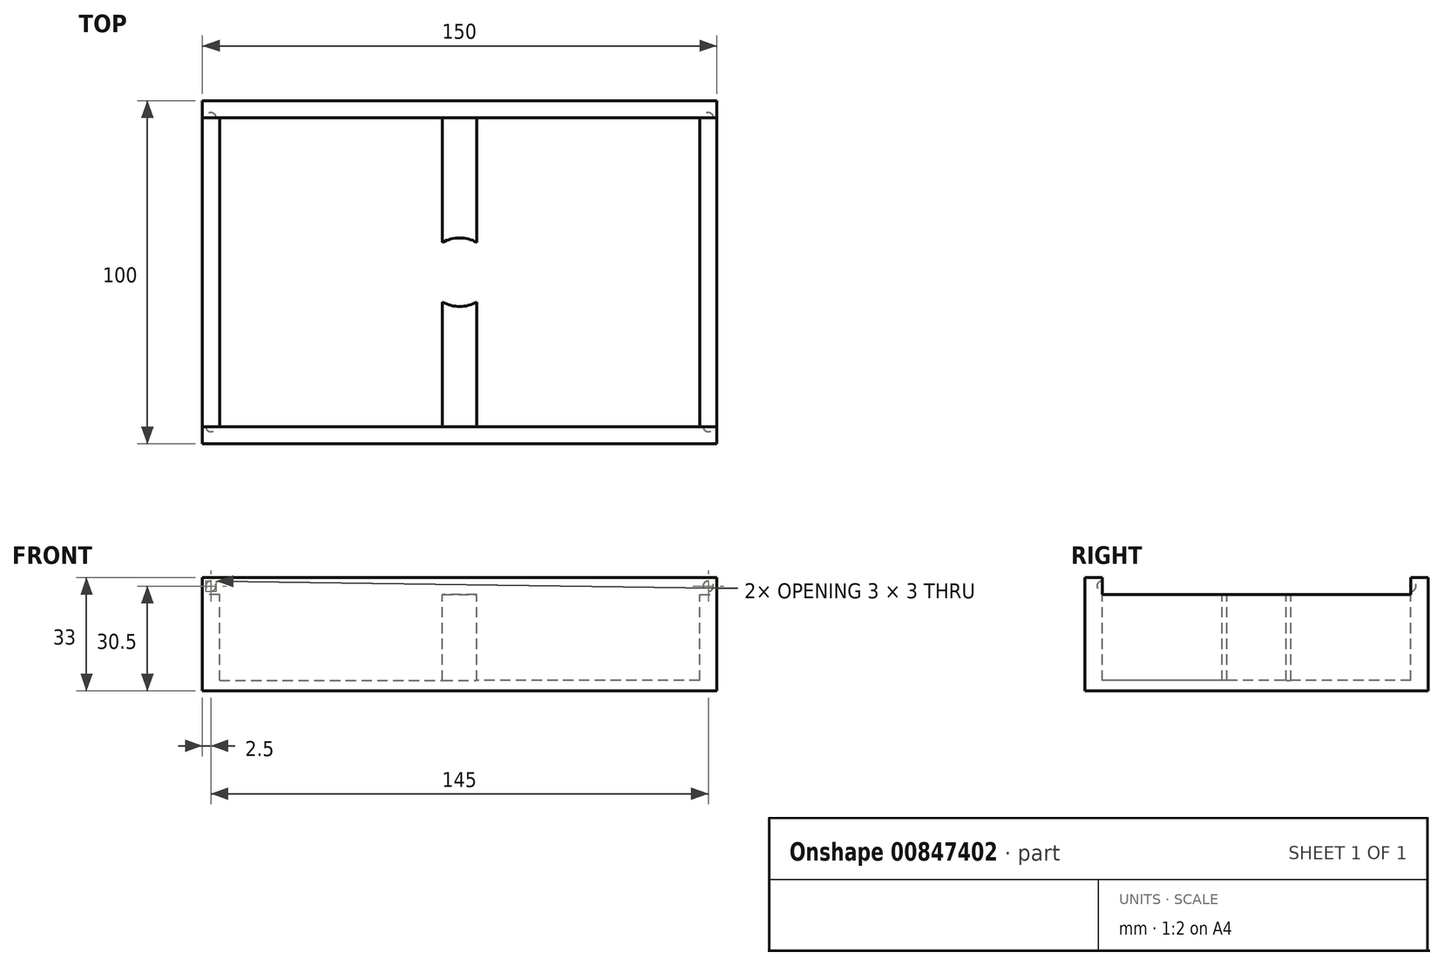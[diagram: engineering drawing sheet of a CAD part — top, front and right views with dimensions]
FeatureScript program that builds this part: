
annotation { "Feature Type Name" : "Feature", "Feature Type Description" : "" }
export const myFeature = defineFeature(function(context is Context, id is Id, definition is map)
    precondition{}
    {
        {
            var Q0;
            Q0=qCreatedBy(makeId("Top.planeOp"),FACE);
            var sketch = newSketch(context, id + "F0", { "sketchPlane" : qUnion([Q0])});
            skLineSegment(sketch, "E0.bottom", {"start": v(75, -50) * mm, "end": v(-75, -50) * mm});
            skLineSegment(sketch, "E0.top", {"start": v(75, 50) * mm, "end": v(-75, 50) * mm});
            skLineSegment(sketch, "E0.left", {"start": v(75, -50) * mm, "end": v(75, 50) * mm});
            skLineSegment(sketch, "E0.right", {"start": v(-75, -50) * mm, "end": v(-75, 50) * mm});
            skPoint(sketch, "E0.middle", {"position": v(0, 0) * mm});
            skSolve(sketch);
        }
        {
            var Q0;
            Q0=qSketchRegion(id+"F0",true);
            extrude(context, id + "F1", {"entities" : qUnion([Q0]), "depth" : 33 * mm, "offsetDistance" : 25 * mm});
        }
        {
            var Q0;
            Q0=makeQuery(id+"F1.opExtrude","CAP_FACE",FACE,{"disambiguationData":[OSD([sQuery(id+"F0.wireOp",EDGE,"E0.bottom"),sQuery(id+"F0.wireOp",EDGE,"E0.top"),sQuery(id+"F0.wireOp",EDGE,"E0.left"),sQuery(id+"F0.wireOp",EDGE,"E0.right")])],"isStart":false});
            var sketch = newSketch(context, id + "F2", { "sketchPlane" : qUnion([Q0])});
            skLineSegment(sketch, "E1.bottom", {"start": v(-70, 45) * mm, "end": v(-5, 45) * mm});
            skLineSegment(sketch, "E1.top", {"start": v(-70, -45) * mm, "end": v(-5, -45) * mm});
            skLineSegment(sketch, "E1.left", {"start": v(-70, 45) * mm, "end": v(-70, -45) * mm});
            skLineSegment(sketch, "E1.right", {"start": v(-5, 45) * mm, "end": v(-5, -45) * mm});
            skPoint(sketch, "E1.middle", {"position": v(-37.5, 0) * mm});
            skPoint(sketch, "E2", {"position": v(0, 50) * mm});
            skPoint(sketch, "E3", {"position": v(-37.5, 50) * mm});
            skLineSegment(sketch, "E4.MirrorCS", {"start": v(70, 45) * mm, "end": v(70, -45) * mm});
            skLineSegment(sketch, "E5.MirrorCS", {"start": v(70, -45) * mm, "end": v(5, -45) * mm});
            skLineSegment(sketch, "E6.MirrorCS", {"start": v(70, 45) * mm, "end": v(5, 45) * mm});
            skLineSegment(sketch, "E7.MirrorCS", {"start": v(5, 45) * mm, "end": v(5, -45) * mm});
            skSolve(sketch);
        }
        {
            var Q0;
            Q0=makeQuery(id+"F2.imprint","IMPRINT",FACE,{"disambiguationData":[TD([[makeQuery(id+"F2.imprint","IMPRINT",EDGE,{"derivedFrom":sQuery(id+"F2.wireOp",EDGE,"E1.bottom")}),-1.0]])]});
            var Q1;
            Q1=makeQuery(id+"F2.imprint","IMPRINT",FACE,{"disambiguationData":[TD([[makeQuery(id+"F2.imprint","IMPRINT",EDGE,{"derivedFrom":sQuery(id+"F2.wireOp",EDGE,"E4.MirrorCS")}),-1.0]])]});
            extrude(context, id + "F3", {"entities" : qUnion([Q0, Q1]), "operationType" : NewBodyOperationType.REMOVE, "oppositeDirection" : true, "depth" : 30 * mm, "offsetDistance" : 25 * mm});
        }
        {
            var Q0;
            Q0=makeQuery(id+"F1.opExtrude","CAP_FACE",FACE,{"disambiguationData":[OSD([sQuery(id+"F0.wireOp",EDGE,"E0.bottom"),sQuery(id+"F0.wireOp",EDGE,"E0.top"),sQuery(id+"F0.wireOp",EDGE,"E0.left"),sQuery(id+"F0.wireOp",EDGE,"E0.right")])],"isStart":false});
            var sketch = newSketch(context, id + "F4", { "sketchPlane" : qUnion([Q0])});
            skLineSegment(sketch, "E8.bottom", {"start": v(-70, 45) * mm, "end": v(-75, 45) * mm});
            skLineSegment(sketch, "E8.top", {"start": v(-70, -45) * mm, "end": v(-75, -45) * mm});
            skLineSegment(sketch, "E8.left", {"start": v(-70, 45) * mm, "end": v(-70, -45) * mm});
            skLineSegment(sketch, "E8.right", {"start": v(-75, 45) * mm, "end": v(-75, -45) * mm});
            skLineSegment(sketch, "E9.bottom", {"start": v(-5, 45) * mm, "end": v(0, 45) * mm});
            skLineSegment(sketch, "E9.top", {"start": v(-5, -45) * mm, "end": v(0, -45) * mm});
            skLineSegment(sketch, "E9.left", {"start": v(-5, 45) * mm, "end": v(-5, -45) * mm});
            skLineSegment(sketch, "E9.right", {"start": v(0, 45) * mm, "end": v(0, -45) * mm});
            skLineSegment(sketch, "E10.MirrorCS", {"start": v(70, 45) * mm, "end": v(70, -45) * mm});
            skLineSegment(sketch, "E11.MirrorCS", {"start": v(70, 45) * mm, "end": v(75, 45) * mm});
            skLineSegment(sketch, "E12.MirrorCS", {"start": v(75, 45) * mm, "end": v(75, -45) * mm});
            skLineSegment(sketch, "E13.MirrorCS", {"start": v(70, -45) * mm, "end": v(75, -45) * mm});
            skLineSegment(sketch, "E14.MirrorCS", {"start": v(5, 45) * mm, "end": v(5, -45) * mm});
            skLineSegment(sketch, "E15.MirrorCS", {"start": v(5, -45) * mm, "end": v(0, -45) * mm});
            skLineSegment(sketch, "E16.MirrorCS", {"start": v(5, 45) * mm, "end": v(0, 45) * mm});
            skSolve(sketch);
        }
        {
            var Q0;
            Q0=qSketchRegion(id+"F4",true);
            extrude(context, id + "F5", {"entities" : qUnion([Q0]), "operationType" : NewBodyOperationType.REMOVE, "oppositeDirection" : true, "depth" : 5 * mm, "offsetDistance" : 25 * mm});
        }
        {
            var Q0;
            Q0=makeQuery(id+"F5.boolean.opBoolean","MERGE",FACE,{"derivedFrom":[makeQuery(id+"F3.boolean.opBoolean","COPY",FACE,{"derivedFrom":makeQuery(id+"F3.opExtrude","SWEPT_FACE",FACE,{"disambiguationData":[OSD([sQuery(id+"F2.wireOp",EDGE,"E1.bottom")])]})}),makeQuery(id+"F3.boolean.opBoolean","COPY",FACE,{"derivedFrom":makeQuery(id+"F3.opExtrude","SWEPT_FACE",FACE,{"disambiguationData":[OSD([sQuery(id+"F2.wireOp",EDGE,"E6.MirrorCS")])]})}),makeQuery(id+"F5.opExtrude","SWEPT_FACE",FACE,{"disambiguationData":[OSD([sQuery(id+"F4.wireOp",EDGE,"E8.bottom")])]}),makeQuery(id+"F5.opExtrude","SWEPT_FACE",FACE,{"disambiguationData":[OSD([sQuery(id+"F4.wireOp",EDGE,"E9.bottom"),sQuery(id+"F4.wireOp",EDGE,"E16.MirrorCS")])]}),makeQuery(id+"F5.opExtrude","SWEPT_FACE",FACE,{"disambiguationData":[OSD([sQuery(id+"F4.wireOp",EDGE,"E11.MirrorCS")])]})]});
            var sketch = newSketch(context, id + "F6", { "sketchPlane" : qUnion([Q0])});
            skPoint(sketch, "E17", {"position": v(-72.5, 30.5) * mm});
            skArc(sketch, "E18", {"start": v(-72.5, 32) * mm, "mid": v(-74, 30.5) * mm, "end": v(-72.5, 29) * mm});
            skLineSegment(sketch, "E19", {"start": v(-72.5, 32) * mm, "end": v(-72.5, 29) * mm});
            skSolve(sketch);
        }
        {
            var Q0;
            Q0=makeQuery(id+"F5.boolean.opBoolean","COPY",FACE,{"derivedFrom":makeQuery(id+"F5.opExtrude","CAP_FACE",FACE,{"disambiguationData":[OSD([sQuery(id+"F4.wireOp",EDGE,"E9.bottom"),sQuery(id+"F4.wireOp",EDGE,"E9.top"),sQuery(id+"F4.wireOp",EDGE,"E9.left"),sQuery(id+"F4.wireOp",EDGE,"E14.MirrorCS"),sQuery(id+"F4.wireOp",EDGE,"E15.MirrorCS"),sQuery(id+"F4.wireOp",EDGE,"E16.MirrorCS")])],"isStart":false})});
            var sketch = newSketch(context, id + "F7", { "sketchPlane" : qUnion([Q0])});
            skCircle(sketch, "E20", {"center": v(0, 0) * mm, "radius": 10 * mm});
            skSolve(sketch);
        }
        {
            var Q0;
            Q0=qSketchRegion(id+"F7",true);
            var Q1;
            Q1=makeQuery(id+"F3.boolean.opBoolean","COPY",FACE,{"derivedFrom":makeQuery(id+"F3.opExtrude","CAP_FACE",FACE,{"disambiguationData":[OSD([sQuery(id+"F2.wireOp",EDGE,"E4.MirrorCS"),sQuery(id+"F2.wireOp",EDGE,"E5.MirrorCS"),sQuery(id+"F2.wireOp",EDGE,"E6.MirrorCS"),sQuery(id+"F2.wireOp",EDGE,"E7.MirrorCS")])],"isStart":false})});
            extrude(context, id + "F8", {"entities" : qUnion([Q0]), "operationType" : NewBodyOperationType.REMOVE, "endBound" : BoundingType.UP_TO_SURFACE, "oppositeDirection" : true, "depth" : 25 * mm, "endBoundEntityFace" : qUnion([Q1]), "offsetDistance" : 25 * mm});
        }
        {
            var Q0;
            Q0=qSketchRegion(id+"F6",true);
            var Q1;
            Q1=sQuery(id+"F6.wireOp",EDGE,"E19");
            revolve(context, id + "F9", {"operationType" : NewBodyOperationType.REMOVE, "surfaceOperationType" : NewSurfaceOperationType.NEW, "entities" : qUnion([Q0]), "axis" : qUnion([Q1]), "revolveType" : RevolveType.FULL, "oppositeDirection" : true});
        }
        {
            var Q0;
            Q0=makeQuery(id+"F1.opExtrude","SWEPT_BODY",BODY,{"disambiguationData":[OSD([sQuery(id+"F0.wireOp",EDGE,"E0.bottom"),sQuery(id+"F0.wireOp",EDGE,"E0.top"),sQuery(id+"F0.wireOp",EDGE,"E0.left"),sQuery(id+"F0.wireOp",EDGE,"E0.right")])]});
            var Q1;
            Q1=qCreatedBy(makeId("Right.planeOp"),FACE);
            mirror(context, id + "F10", {"operationType" : NewBodyOperationType.INTERSECT, "entities" : qUnion([Q0]), "mirrorPlane" : qUnion([Q1])});
        }
        {
            var Q0;
            Q0=makeQuery(id+"F1.opExtrude","SWEPT_BODY",BODY,{"disambiguationData":[OSD([sQuery(id+"F0.wireOp",EDGE,"E0.bottom"),sQuery(id+"F0.wireOp",EDGE,"E0.top"),sQuery(id+"F0.wireOp",EDGE,"E0.left"),sQuery(id+"F0.wireOp",EDGE,"E0.right")])]});
            var Q1;
            Q1=qCreatedBy(makeId("Front.planeOp"),FACE);
            mirror(context, id + "F11", {"operationType" : NewBodyOperationType.INTERSECT, "entities" : qUnion([Q0]), "mirrorPlane" : qUnion([Q1])});
        }
    });
